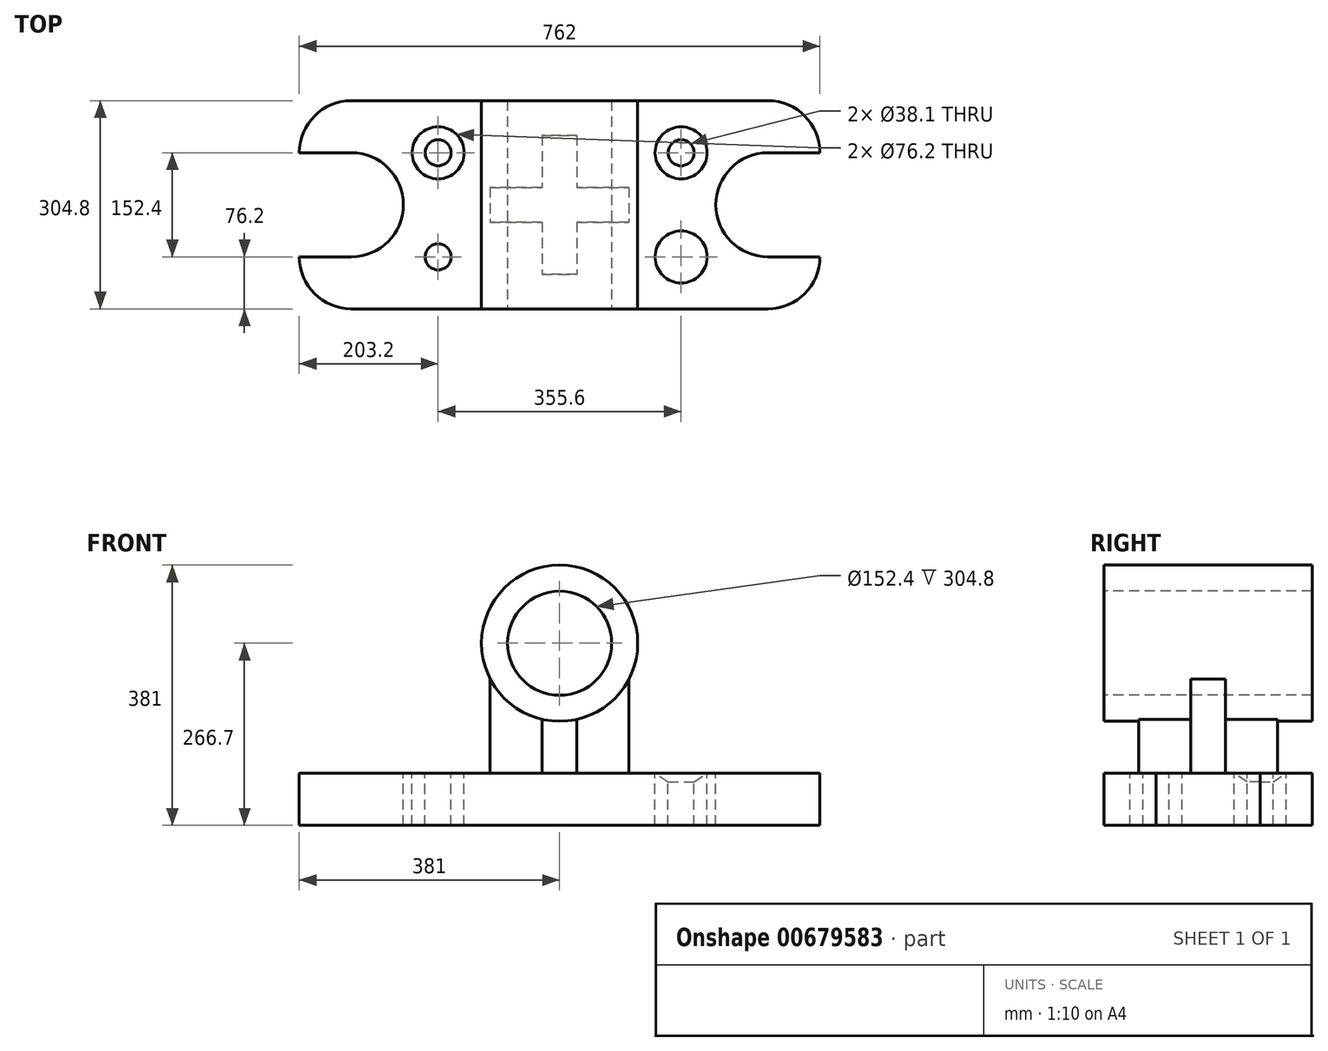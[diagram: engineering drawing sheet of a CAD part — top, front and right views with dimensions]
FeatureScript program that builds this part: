
annotation { "Feature Type Name" : "Feature", "Feature Type Description" : "" }
export const myFeature = defineFeature(function(context is Context, id is Id, definition is map)
    precondition{}
    {
        {
            var Q0;
            Q0=qCreatedBy(makeId("Top.planeOp"),FACE);
            var sketch = newSketch(context, id + "F0", { "sketchPlane" : qUnion([Q0])});
            skLineSegment(sketch, "E0.bottom", {"start": v(304.8, -152.4) * mm, "end": v(-304.8, -152.4) * mm});
            skLineSegment(sketch, "E0.top", {"start": v(304.8, 152.4) * mm, "end": v(-304.8, 152.4) * mm});
            skLineSegment(sketch, "E0.left", {"start": v(381, -76.2) * mm, "end": v(381, 152.4) * mm});
            skLineSegment(sketch, "E0.right", {"start": v(-381, -152.4) * mm, "end": v(-381, 152.4) * mm});
            skPoint(sketch, "E0.middle", {"position": v(0, 0) * mm});
            skLineSegment(sketch, "E1.bottom", {"start": v(101.6, -25.4) * mm, "end": v(-101.6, -25.4) * mm});
            skLineSegment(sketch, "E1.top", {"start": v(101.6, 25.4) * mm, "end": v(-101.6, 25.4) * mm});
            skLineSegment(sketch, "E1.left", {"start": v(101.6, -25.4) * mm, "end": v(101.6, 25.4) * mm});
            skLineSegment(sketch, "E1.right", {"start": v(-101.6, -25.4) * mm, "end": v(-101.6, 25.4) * mm});
            skLineSegment(sketch, "E2.bottom", {"start": v(25.4, -101.6) * mm, "end": v(-25.4, -101.6) * mm});
            skLineSegment(sketch, "E2.top", {"start": v(25.4, 101.6) * mm, "end": v(-25.4, 101.6) * mm});
            skLineSegment(sketch, "E2.left", {"start": v(25.4, -101.6) * mm, "end": v(25.4, 101.6) * mm});
            skLineSegment(sketch, "E2.right", {"start": v(-25.4, -101.6) * mm, "end": v(-25.4, 101.6) * mm});
            skLineSegment(sketch, "E3", {"start": v(381, 76.2) * mm, "end": v(381, 76.2) * mm});
            skLineSegment(sketch, "E4", {"start": v(381, 76.2) * mm, "end": v(304.8, 76.2) * mm});
            skLineSegment(sketch, "E5", {"start": v(228.6, 0) * mm, "end": v(228.6, 0) * mm});
            skLineSegment(sketch, "E6", {"start": v(304.8, -76.2) * mm, "end": v(381, -76.2) * mm});
            skPoint(sketch, "E7.visualSharp", {"position": v(228.6, 76.2) * mm});
            skArc(sketch, "E7.filletArc", {"start": v(304.8, 76.2) * mm, "mid": v(250.92, 53.88) * mm, "end": v(228.6, 0) * mm});
            skPoint(sketch, "E8.visualSharp", {"position": v(228.6, -76.2) * mm});
            skArc(sketch, "E8.filletArc", {"start": v(228.6, 0) * mm, "mid": v(250.92, -53.88) * mm, "end": v(304.8, -76.2) * mm});
            skArc(sketch, "E9.MirrorCS", {"start": v(-228.6, 0) * mm, "mid": v(-250.92, -53.88) * mm, "end": v(-304.8, -76.2) * mm});
            skPoint(sketch, "E10.MirrorP", {"position": v(-228.6, -76.2) * mm});
            skPoint(sketch, "E11.MirrorP", {"position": v(-228.6, 76.2) * mm});
            skLineSegment(sketch, "E12.MirrorCS", {"start": v(-381, 76.2) * mm, "end": v(-381, 76.2) * mm});
            skLineSegment(sketch, "E13.MirrorCS", {"start": v(-381, 76.2) * mm, "end": v(-304.8, 76.2) * mm});
            skLineSegment(sketch, "E14.MirrorCS", {"start": v(-381, -76.2) * mm, "end": v(-381, 152.4) * mm});
            skLineSegment(sketch, "E15.MirrorCS", {"start": v(-304.8, -76.2) * mm, "end": v(-381, -76.2) * mm});
            skArc(sketch, "E16.MirrorCS", {"start": v(-304.8, 76.2) * mm, "mid": v(-250.92, 53.88) * mm, "end": v(-228.6, 0) * mm});
            skLineSegment(sketch, "E17", {"start": v(228.6, 0) * mm, "end": v(177.8, 0) * mm});
            skLineSegment(sketch, "E18", {"start": v(177.8, 0) * mm, "end": v(177.8, 76.2) * mm});
            skCircle(sketch, "E19", {"center": v(177.8, 76.2) * mm, "radius": 19.05 * mm});
            skCircle(sketch, "E20", {"center": v(177.8, 76.2) * mm, "radius": 38.1 * mm});
            skCircle(sketch, "E21.MirrorC", {"center": v(177.8, -76.2) * mm, "radius": 38.1 * mm});
            skCircle(sketch, "E22.MirrorC", {"center": v(177.8, -76.2) * mm, "radius": 19.05 * mm});
            skCircle(sketch, "E23.MirrorC", {"center": v(-177.8, -76.2) * mm, "radius": 19.05 * mm});
            skCircle(sketch, "E24.MirrorC", {"center": v(-177.8, -76.2) * mm, "radius": 38.1 * mm});
            skCircle(sketch, "E25.MirrorC", {"center": v(-177.8, 76.2) * mm, "radius": 19.05 * mm});
            skCircle(sketch, "E26.MirrorC", {"center": v(-177.8, 76.2) * mm, "radius": 38.1 * mm});
            skPoint(sketch, "E27.visualSharp", {"position": v(381, 152.4) * mm});
            skArc(sketch, "E27.filletArc", {"start": v(381, 76.2) * mm, "mid": v(358.68, 130.08) * mm, "end": v(304.8, 152.4) * mm});
            skPoint(sketch, "E28.visualSharp", {"position": v(381, -152.4) * mm});
            skArc(sketch, "E28.filletArc", {"start": v(304.8, -152.4) * mm, "mid": v(358.68, -130.08) * mm, "end": v(381, -76.2) * mm});
            skPoint(sketch, "E29.visualSharp", {"position": v(-381, 152.4) * mm});
            skArc(sketch, "E29.filletArc", {"start": v(-304.8, 152.4) * mm, "mid": v(-358.68, 130.08) * mm, "end": v(-381, 76.2) * mm});
            skPoint(sketch, "E30.visualSharp", {"position": v(-381, -152.4) * mm});
            skArc(sketch, "E30.filletArc", {"start": v(-381, -76.2) * mm, "mid": v(-358.68, -130.08) * mm, "end": v(-304.8, -152.4) * mm});
            skLineSegment(sketch, "E31", {"start": v(228.6, -76.2) * mm, "end": v(-228.6, -76.2) * mm});
            skSolve(sketch);
        }
        {
            var Q0;
            Q0=makeQuery(id+"F0.imprint","IMPRINT",FACE,{"disambiguationData":[TD([[makeQuery(id+"F0.imprint","IMPRINT",EDGE,{"derivedFrom":sQuery(id+"F0.wireOp",EDGE,"E0.bottom")}),-1.0]])]});
            var Q1;
            {var subQ0=sQuery(id+"F0.wireOp",EDGE,"E1.right");Q1=makeQuery(id+"F0.imprint","IMPRINT",FACE,{"disambiguationData":[TD([[makeQuery(id+"F0.imprint","IMPRINT",EDGE,{"derivedFrom":subQ0}),-1.0]])]});}
            var Q2;
            {var subQ5=sQuery(id+"F0.wireOp",EDGE,"E2.top");Q2=makeQuery(id+"F0.imprint","IMPRINT",FACE,{"disambiguationData":[TD([[makeQuery(id+"F0.imprint","IMPRINT",EDGE,{"derivedFrom":subQ5}),1.0]])]});}
            var Q3;
            {var subQ0=sQuery(id+"F0.wireOp",EDGE,"E1.left");Q3=makeQuery(id+"F0.imprint","IMPRINT",FACE,{"disambiguationData":[TD([[makeQuery(id+"F0.imprint","IMPRINT",EDGE,{"derivedFrom":subQ0}),1.0]])]});}
            var Q4;
            {var subQ0=sQuery(id+"F0.wireOp",EDGE,"E2.left");var subQ1=sQuery(id+"F0.wireOp",EDGE,"E1.bottom");var subQ2=makeQuery(id+"F0.imprint","INTERSECT",VERTEX,{"derivedFrom":[subQ1,subQ0]});Q4=makeQuery(id+"F0.imprint","IMPRINT",FACE,{"disambiguationData":[TD([[makeQuery(id+"F0.imprint","IMPRINT",EDGE,{"disambiguationData":[TD([[subQ2,-1.0]])],"derivedFrom":subQ1}),-1.0]])]});}
            var Q5;
            {var subQ5=sQuery(id+"F0.wireOp",EDGE,"E2.bottom");Q5=makeQuery(id+"F0.imprint","IMPRINT",FACE,{"disambiguationData":[TD([[makeQuery(id+"F0.imprint","IMPRINT",EDGE,{"derivedFrom":subQ5}),-1.0]])]});}
            var Q6;
            Q6=makeQuery(id+"F0.imprint","IMPRINT",FACE,{"disambiguationData":[TD([[makeQuery(id+"F0.imprint","IMPRINT",EDGE,{"derivedFrom":sQuery(id+"F0.wireOp",EDGE,"E21.MirrorC")}),-1.0]])]});
            var Q7;
            Q7=makeQuery(id+"F0.imprint","IMPRINT",FACE,{"disambiguationData":[TD([[makeQuery(id+"F0.imprint","IMPRINT",EDGE,{"derivedFrom":sQuery(id+"F0.wireOp",EDGE,"E19")}),-1.0]])]});
            var Q8;
            Q8=makeQuery(id+"F0.imprint","IMPRINT",FACE,{"disambiguationData":[TD([[makeQuery(id+"F0.imprint","IMPRINT",EDGE,{"derivedFrom":sQuery(id+"F0.wireOp",EDGE,"E25.MirrorC")}),1.0]])]});
            var Q9;
            Q9=makeQuery(id+"F0.imprint","IMPRINT",FACE,{"disambiguationData":[TD([[makeQuery(id+"F0.imprint","IMPRINT",EDGE,{"derivedFrom":sQuery(id+"F0.wireOp",EDGE,"E23.MirrorC")}),-1.0]])]});
            var Q10;
            {var subQ0=sQuery(id+"F0.wireOp",EDGE,"E2.left");var subQ1=sQuery(id+"F0.wireOp",EDGE,"E1.bottom");var subQ2=makeQuery(id+"F0.imprint","INTERSECT",VERTEX,{"derivedFrom":[subQ1,subQ0]});Q10=makeQuery(id+"F0.imprint","IMPRINT",FACE,{"disambiguationData":[TD([[makeQuery(id+"F0.imprint","IMPRINT",EDGE,{"disambiguationData":[TD([[subQ2,-1.0]])],"derivedFrom":subQ1}),1.0]])]});}
            extrude(context, id + "F1", {"entities" : qUnion([Q0, Q1, Q2, Q3, Q4, Q5, Q6, Q7, Q8, Q9, Q10]), "oppositeDirection" : true, "depth" : 76.2 * mm, "offsetDistance" : 25.4 * mm});
        }
        {
            var Q0;
            Q0=makeQuery(id+"F1.opExtrude","SWEPT_FACE",FACE,{"disambiguationData":[OSD([sQuery(id+"F0.wireOp",EDGE,"E4")])]});
            var sketch = newSketch(context, id + "F2", { "sketchPlane" : qUnion([Q0])});
            skLineSegment(sketch, "E32", {"start": v(0, 0) * mm, "end": v(177.8, 0) * mm});
            skLineSegment(sketch, "E33", {"start": v(177.8, 0) * mm, "end": v(215.9, 0) * mm});
            skLineSegment(sketch, "E34", {"start": v(177.8, 0) * mm, "end": v(177.8, -12.7) * mm});
            skLineSegment(sketch, "E35", {"start": v(177.8, -12.7) * mm, "end": v(196.85, -12.7) * mm});
            skLineSegment(sketch, "E36", {"start": v(196.85, -12.7) * mm, "end": v(215.9, 0) * mm});
            skSolve(sketch);
        }
        {
            var Q0;
            Q0=makeQuery(id+"F2.imprint","IMPRINT",FACE,{"disambiguationData":[TD([[makeQuery(id+"F2.imprint","IMPRINT",EDGE,{"derivedFrom":sQuery(id+"F2.wireOp",EDGE,"E33")}),-1.0]])]});
            var Q1;
            Q1=sQuery(id+"F2.wireOp",EDGE,"E34");
            revolve(context, id + "F3", {"operationType" : NewBodyOperationType.REMOVE, "entities" : qUnion([Q0]), "axis" : qUnion([Q1]), "revolveType" : RevolveType.FULL, "oppositeDirection" : true});
        }
        {
            var Q0;
            {var subQ0=sQuery(id+"F0.wireOp",EDGE,"E1.right");Q0=makeQuery(id+"F0.imprint","IMPRINT",FACE,{"disambiguationData":[TD([[makeQuery(id+"F0.imprint","IMPRINT",EDGE,{"derivedFrom":subQ0}),-1.0]])]});}
            var Q1;
            {var subQ0=sQuery(id+"F0.wireOp",EDGE,"E2.left");var subQ1=sQuery(id+"F0.wireOp",EDGE,"E1.bottom");var subQ2=makeQuery(id+"F0.imprint","INTERSECT",VERTEX,{"derivedFrom":[subQ1,subQ0]});Q1=makeQuery(id+"F0.imprint","IMPRINT",FACE,{"disambiguationData":[TD([[makeQuery(id+"F0.imprint","IMPRINT",EDGE,{"disambiguationData":[TD([[subQ2,-1.0]])],"derivedFrom":subQ1}),-1.0]])]});}
            var Q2;
            {var subQ5=sQuery(id+"F0.wireOp",EDGE,"E2.top");Q2=makeQuery(id+"F0.imprint","IMPRINT",FACE,{"disambiguationData":[TD([[makeQuery(id+"F0.imprint","IMPRINT",EDGE,{"derivedFrom":subQ5}),1.0]])]});}
            var Q3;
            {var subQ0=sQuery(id+"F0.wireOp",EDGE,"E1.left");Q3=makeQuery(id+"F0.imprint","IMPRINT",FACE,{"disambiguationData":[TD([[makeQuery(id+"F0.imprint","IMPRINT",EDGE,{"derivedFrom":subQ0}),1.0]])]});}
            var Q4;
            {var subQ0=sQuery(id+"F0.wireOp",EDGE,"E2.left");var subQ1=sQuery(id+"F0.wireOp",EDGE,"E1.bottom");var subQ2=makeQuery(id+"F0.imprint","INTERSECT",VERTEX,{"derivedFrom":[subQ1,subQ0]});Q4=makeQuery(id+"F0.imprint","IMPRINT",FACE,{"disambiguationData":[TD([[makeQuery(id+"F0.imprint","IMPRINT",EDGE,{"disambiguationData":[TD([[subQ2,-1.0]])],"derivedFrom":subQ1}),1.0]])]});}
            var Q5;
            {var subQ0=sQuery(id+"F0.wireOp",EDGE,"E2.bottom");Q5=makeQuery(id+"F0.imprint","IMPRINT",FACE,{"disambiguationData":[TD([[makeQuery(id+"F0.imprint","IMPRINT",EDGE,{"derivedFrom":subQ0}),-1.0]])]});}
            extrude(context, id + "F4", {"entities" : qUnion([Q0, Q1, Q2, Q3, Q4, Q5]), "operationType" : NewBodyOperationType.ADD, "depth" : 190.5 * mm, "offsetDistance" : 25.4 * mm});
        }
        {
            var Q0;
            Q0=makeQuery(id+"F4.opExtrude","CAP_FACE",FACE,{"disambiguationData":[OSD([sQuery(id+"F0.wireOp",EDGE,"E1.bottom"),sQuery(id+"F0.wireOp",EDGE,"E1.top"),sQuery(id+"F0.wireOp",EDGE,"E1.left"),sQuery(id+"F0.wireOp",EDGE,"E1.right"),sQuery(id+"F0.wireOp",EDGE,"E2.bottom"),sQuery(id+"F0.wireOp",EDGE,"E2.top"),sQuery(id+"F0.wireOp",EDGE,"E2.left"),sQuery(id+"F0.wireOp",EDGE,"E2.right")])],"isStart":false});
            var sketch = newSketch(context, id + "F5", { "sketchPlane" : qUnion([Q0])});
            skLineSegment(sketch, "E37", {"start": v(0, 0) * mm, "end": v(0, 152.4) * mm});
            skPoint(sketch, "E37.endSnap0", {"position": v(0, 101.6) * mm});
            skLineSegment(sketch, "E38", {"start": v(0, 152.4) * mm, "end": v(114.3, 152.4) * mm});
            skLineSegment(sketch, "E39", {"start": v(114.3, 152.4) * mm, "end": v(114.3, -152.4) * mm});
            skLineSegment(sketch, "E40", {"start": v(0, -152.4) * mm, "end": v(0, 0) * mm});
            skLineSegment(sketch, "E41", {"start": v(114.3, -152.4) * mm, "end": v(76.2, -152.4) * mm});
            skLineSegment(sketch, "E42", {"start": v(76.2, -152.4) * mm, "end": v(0, -152.4) * mm});
            skLineSegment(sketch, "E43", {"start": v(76.2, -152.4) * mm, "end": v(76.2, 152.4) * mm});
            skSolve(sketch);
        }
        {
            var Q0;
            {var subQ8=sQuery(id+"F5.wireOp",EDGE,"E39");Q0=makeQuery(id+"F5.imprint","IMPRINT",FACE,{"disambiguationData":[TD([[makeQuery(id+"F5.imprint","IMPRINT",EDGE,{"derivedFrom":subQ8}),-1.0]])]});}
            var Q1;
            {var subQ1=sQuery(id+"F0.wireOp",EDGE,"E1.left");var subQ9=makeQuery(id+"F4.opExtrude","CAP_EDGE",EDGE,{"disambiguationData":[OSD([subQ1])],"isStart":false});Q1=makeQuery(id+"F5.imprint","IMPRINT",FACE,{"disambiguationData":[TD([[makeQuery(id+"F5.imprint","IMPRINT",EDGE,{"derivedFrom":subQ9}),1.0]])]});}
            var Q2;
            Q2=sQuery(id+"F5.wireOp",EDGE,"E37");
            revolve(context, id + "F6", {"operationType" : NewBodyOperationType.ADD, "entities" : qUnion([Q0, Q1]), "axis" : qUnion([Q2]), "revolveType" : RevolveType.FULL});
        }
        {
            var Q0;
            {var subQ0=sQuery(id+"F0.wireOp",EDGE,"E2.left");var subQ1=sQuery(id+"F0.wireOp",EDGE,"E2.top");var subQ4=makeQuery(id+"F4.opExtrude","CAP_EDGE",EDGE,{"disambiguationData":[OSD([subQ0]),TDD([makeQuery(id+"F0.imprint","IMPRINT",EDGE,{"disambiguationData":[TD([[makeQuery(id+"F0.imprint","INTERSECT",VERTEX,{"derivedFrom":[subQ1,subQ0]}),1.0]])],"derivedFrom":subQ0})])],"isStart":false});Q0=makeQuery(id+"F5.imprint","IMPRINT",FACE,{"disambiguationData":[TD([[makeQuery(id+"F5.imprint","IMPRINT",EDGE,{"derivedFrom":subQ4}),-1.0]])]});}
            var Q1;
            {var subQ0=sQuery(id+"F0.wireOp",EDGE,"E2.left");var subQ6=sQuery(id+"F0.wireOp",EDGE,"E2.top");var subQ9=makeQuery(id+"F4.opExtrude","CAP_EDGE",EDGE,{"disambiguationData":[OSD([subQ0]),TDD([makeQuery(id+"F0.imprint","IMPRINT",EDGE,{"disambiguationData":[TD([[makeQuery(id+"F0.imprint","INTERSECT",VERTEX,{"derivedFrom":[subQ6,subQ0]}),1.0]])],"derivedFrom":subQ0})])],"isStart":false});Q1=makeQuery(id+"F5.imprint","IMPRINT",FACE,{"disambiguationData":[TD([[makeQuery(id+"F5.imprint","IMPRINT",EDGE,{"derivedFrom":subQ9}),1.0]])]});}
            var Q2;
            {var subQ6=sQuery(id+"F5.wireOp",EDGE,"E42");Q2=makeQuery(id+"F5.imprint","IMPRINT",FACE,{"disambiguationData":[TD([[makeQuery(id+"F5.imprint","IMPRINT",EDGE,{"derivedFrom":subQ6}),-1.0]])]});}
            var Q3;
            Q3=makeQuery(id+"F6.opRevolve","SWEPT_FACE",FACE,{"disambiguationData":[OSD([sQuery(id+"F5.wireOp",EDGE,"E39")])]});
            revolve(context, id + "F7", {"operationType" : NewBodyOperationType.REMOVE, "entities" : qUnion([Q0, Q1, Q2]), "axis" : qUnion([Q3]), "revolveType" : RevolveType.FULL, "oppositeDirection" : true});
        }
    });
